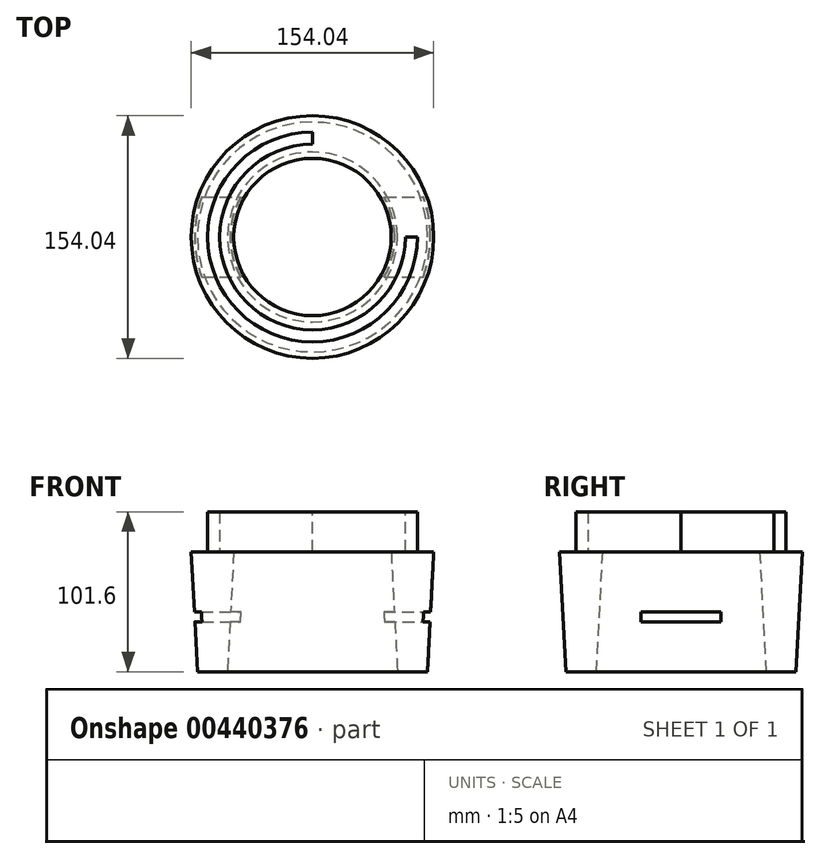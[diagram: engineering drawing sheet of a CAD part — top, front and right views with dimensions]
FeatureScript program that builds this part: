
annotation { "Feature Type Name" : "Feature", "Feature Type Description" : "" }
export const myFeature = defineFeature(function(context is Context, id is Id, definition is map)
    precondition{}
    {
        {
            var Q0;
            Q0=qCreatedBy(makeId("Top.planeOp"),FACE);
            var sketch = newSketch(context, id + "F0", { "sketchPlane" : qUnion([Q0])});
            skCircle(sketch, "E0", {"center": v(0, 0) * mm, "radius": 53.98 * mm});
            skCircle(sketch, "E1.0", {"center": v(0, 0) * mm, "radius": 73.03 * mm});
            skSolve(sketch);
        }
        {
            var Q0;
            Q0 = qSketchRegion(id + "F0", true);
            extrude(context, id + "F1", {"entities" : qUnion([Q0]), "depth" : 76.2 * mm, "hasDraft" : true, "draftAngle" : 3 * degree});
        }
        {
            var Q0;
            Q0=makeQuery(id+"F1.opExtrude","CAP_FACE",FACE,{"disambiguationData":[OSD([sQuery(id+"F0.wireOp",EDGE,"E0"),sQuery(id+"F0.wireOp",EDGE,"E1.0")])],"isStart":false});
            var sketch = newSketch(context, id + "F2", { "sketchPlane" : qUnion([Q0])});
            skCircle(sketch, "E2", {"center": v(0, 0) * mm, "radius": 58.95 * mm});
            skCircle(sketch, "E3", {"center": v(0, 0) * mm, "radius": 66.61 * mm});
            skSolve(sketch);
        }
        {
            var Q0;
            Q0=makeQuery(id+"F2.imprint","IMPRINT",FACE,{"disambiguationData":[TD([[makeQuery(id+"F2.imprint","IMPRINT",EDGE,{"derivedFrom":sQuery(id+"F2.wireOp",EDGE,"E2")}),-1.0]])]});
            extrude(context, id + "F3", {"entities" : qUnion([Q0]), "depth" : 25.4 * mm});
        }
        {
            var Q0;
            Q0=makeQuery(id+"F3.opExtrude","CAP_FACE",FACE,{"disambiguationData":[OSD([sQuery(id+"F2.wireOp",EDGE,"E2"),sQuery(id+"F2.wireOp",EDGE,"E3")])],"isStart":false});
            var sketch = newSketch(context, id + "F4", { "sketchPlane" : qUnion([Q0])});
            skArc(sketch, "E4.0", {"start": v(58.95, 0) * mm, "mid": v(41.69, 41.69) * mm, "end": v(0, 58.95) * mm});
            skArc(sketch, "E5.0", {"start": v(66.61, 0) * mm, "mid": v(47.1, 47.1) * mm, "end": v(0, 66.61) * mm});
            skLineSegment(sketch, "E6", {"start": v(0, 66.61) * mm, "end": v(0, 58.95) * mm});
            skLineSegment(sketch, "E7", {"start": v(58.95, 0) * mm, "end": v(66.61, 0) * mm});
            skSolve(sketch);
        }
        {
            var Q0;
            Q0 = qSketchRegion(id + "F4", true);
            extrude(context, id + "F5", {"entities" : qUnion([Q0]), "operationType" : NewBodyOperationType.REMOVE, "oppositeDirection" : true, "depth" : 25.4 * mm});
        }
        {
            var Q0;
            Q0=qCreatedBy(makeId("Right.planeOp"),FACE);
            var sketch = newSketch(context, id + "F6", { "sketchPlane" : qUnion([Q0])});
            skLineSegment(sketch, "E8.bottom", {"start": v(25.4, 31.75) * mm, "end": v(-25.4, 31.75) * mm});
            skLineSegment(sketch, "E8.top", {"start": v(25.4, 38.1) * mm, "end": v(-25.4, 38.1) * mm});
            skLineSegment(sketch, "E8.left", {"start": v(25.4, 31.75) * mm, "end": v(25.4, 38.1) * mm});
            skLineSegment(sketch, "E8.right", {"start": v(-25.4, 31.75) * mm, "end": v(-25.4, 38.1) * mm});
            skPoint(sketch, "E8.middle", {"position": v(0, 34.93) * mm});
            skSolve(sketch);
        }
        {
            var Q0;
            Q0 = qSketchRegion(id + "F6", true);
            extrude(context, id + "F7", {"entities" : qUnion([Q0]), "operationType" : NewBodyOperationType.REMOVE, "endBound" : BoundingType.SYMMETRIC, "oppositeDirection" : true, "depth" : 254 * mm});
        }
    });
